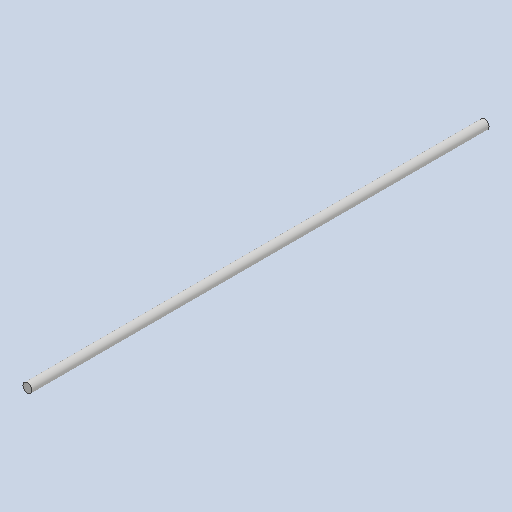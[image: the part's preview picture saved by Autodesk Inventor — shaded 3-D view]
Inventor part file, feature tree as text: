
AUTODESK INVENTOR PART (.ipt)
format: ipt  version: 2023 (Build 270158000, 158)  size: 81,920 bytes
history: native  units: mm
features: extrude x1, sketch x1
ambient origin geometry x8: Origin, YZ Plane, XZ Plane, XY Plane, X Axis, Y Axis, Z Axis, Center Point
bodies: Solid1 (feature_tree)
feature tree (2):
  extrude  "Extrusion1"  Depth=400.0mm
  sketch  "Sketch1"  dims[d0=8.0mm d1=400.0mm d2=0.0mm]
